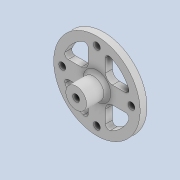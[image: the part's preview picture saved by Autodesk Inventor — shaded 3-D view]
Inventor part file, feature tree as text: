
AUTODESK INVENTOR PART (.ipt)
format: ipt  version: 2020 (Build 240168000, 168)  size: 248,832 bytes
history: native  units: mm
features: sketch x5, extrude x4, other x4, fillet x3, projected_geometry x2, hole x1, pattern_circular x1, reference x1
ambient origin geometry x8: Origin, YZ Plane, XZ Plane, XY Plane, X Axis, Y Axis, Z Axis, Center Point
bodies: Solid1 (feature_tree)
feature tree (21):
  extrude  "Extrusion1"  Depth=5.0mm
  hole  "Hole1"  [1 undecoded]
  extrude  "Extrusion2"  Depth=2.0mm
  fillet  "Fillet1"  Radius=1.0mm
  fillet  "Fillet2"  Radius=2.0mm
  extrude  "Extrusion3"  Depth=1.0mm
  extrude  "Extrusion4"  Depth=1.0mm
  pattern_circular  "Circular Pattern1"  [2 undecoded]
  fillet  "Fillet3"  Radius=40.0mm
  sketch  "Sketch1"  dims[d0=5.0mm d1=5.0mm]
  reference  "Reference1"
  sketch  "Sketch2"  dims[d2=2.0mm d3=0.0mm]
  projected_geometry  "Projected Loop1"
  sketch  "Sketch3"  dims[d4=2.0mm d5=6.0mm d6=4.0mm d7=2.0mm d8=90.0deg d9=5.0mm d10=0.0mm d11=6.0mm]
  sketch  "Sketch4"  dims[d12=6.0mm d13=0.0mm d14=2.0mm d15=1.0mm d16=2.0mm]
  sketch  "Sketch5"  dims[d17=12.0mm d18=0.0mm d19=25.0mm d20=20.0mm d21=2.0mm d22=0.0mm d23=40.0mm d24=360.0deg d26=1.0mm]
  projected_geometry  "Projected Loop2"
  parser-record x1  (decoder bookkeeping rows leaked as tree rows — omitted from the tree; the rows remain in map.json)
  other  "reducer_1.iam"
  other  "mot_27_ass:1"
  other  "mot_27_1:1"
note: 3 required parameter values undecoded (feature->parameter linkage not recoverable at this tier; creation-order binding heuristic only, values carry confidence <= 0.55)
note: 1 file-system path scrubbed to <path> (originals preserved in map.json)
